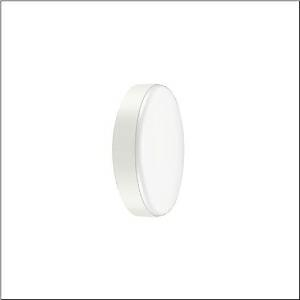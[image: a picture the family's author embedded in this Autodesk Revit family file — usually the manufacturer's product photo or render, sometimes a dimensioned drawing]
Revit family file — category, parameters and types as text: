
# Revit family: rondel_31_51wc10ma32a
name_source: partatom
category: Lighting Fixtures
units: mm (PartAtom-declared; Revit-internal decimal feet)

## family parameters
Cut with Voids When Loaded = No
Host = Face
Light Source = No
Part Type = Normal
Room Calculation Point = No
Round Connector Dimension = Use Diameter
Shared = No

## types (1)
- --- (1 x LED, 2450 lm, 19 W, 3000K)
    Apparent Load = 19 VA
    CIE Flux Codes = 44 75 94 94 100
    Color Rendering = 80
    Color Temperature = 3000K
    Default Elevation = 1800 mm
    Description = Rondel 31, wall and ceiling luminaire, primary optical cover: cover, of PC, opal, light emission: direct distribution, primary light characteristic: symmetric, installation type: surface-mounted, LED, rated luminous flux: 2.300lm, luminous efficacy: 120lm/W, light colour: 830, colour temperature: 3000K, with terminal, 3-pole, max. 2.5mm², mains connection: 220..240V, AC, 50/60Hz, rated input power: 19W, luminaire housing, of PC, traffic white (RAL 9016), diameter: 350mm, protection rating (complete): IP65, insulation class (complete): insulation class II (safety insulation), certification: CE, impact resistance: IK10, permissible storage temperature: -20..+60°C, packaging unit: 1 piece
    Height = 97 mm
    Lamp = 1 x LED
    Lamp Light Flux = 2450 lm
    Lamp Power = 19 W
    Lamp count = 1
    Length = 350 mm
    Luminous efficacy = 129 lm/W
    Manufacturer = Siteco
    ModVariant = No
    Model = 51WC10MA32A
    Mounting Place = Ceiling
    Mounting Type = Surface mounted
    Number of Poles = 1
    OnlyDefault = Yes
    Power Factor = 1
    Product Name = Rondel 31
    Product group = wall and ceiling luminaire
    ProductGroupID = 301
    Protection Class = Protection class II
    Protection Degree = IP 65
    RLX_Detail_Level = 1
    RlxData = <blob elided: 30381 chars, md5=a581feb7>
    Socket = socket
    Standby Power = 0 W
    System Light Flux = 2450 lm
    System Power = 19 W
    Type Comments = factory setting: luminous flux: 100 % | (ON | ON)
    Type Image = l_1007027.jpg
    URL = http://relux.com
    VarID = @adj_060589
    Voltage = 0 V
    Weight = 0.00 kg
    Width = 0 mm  [stored 0 ft]

note: [stored X ft] marks values corroborated as IEEE doubles in the binary element streams (Revit-internal decimal feet)

## geometry (parser evidence)
native form markers: Blend x4, Sweep x15
no freeform markers — native parametric forms only
